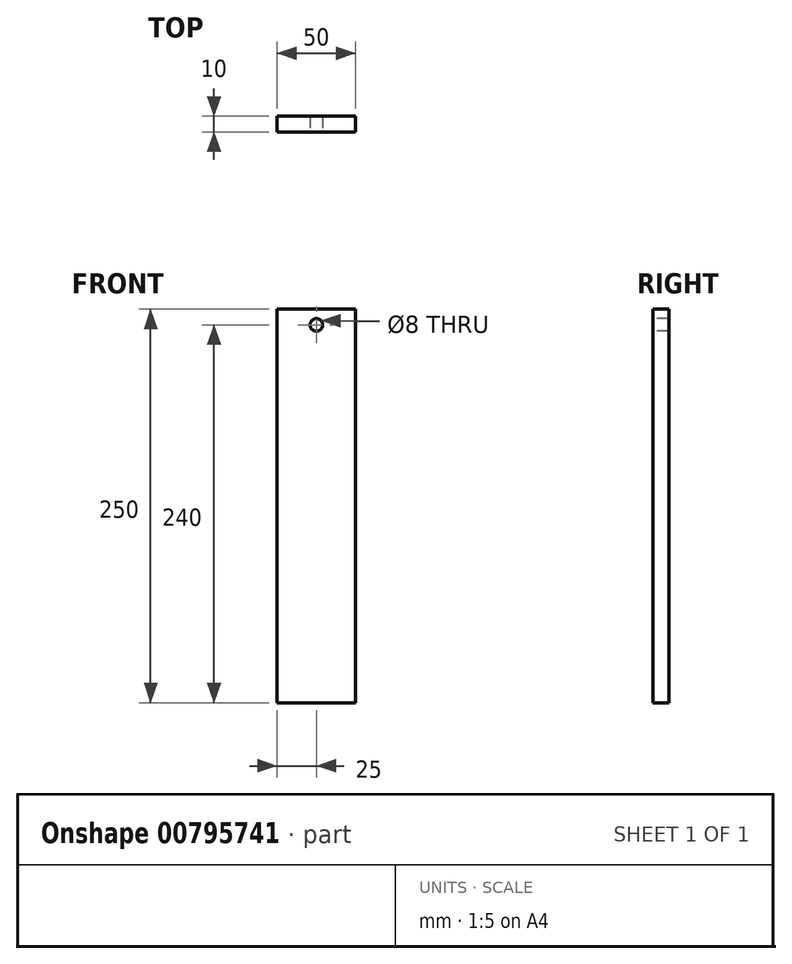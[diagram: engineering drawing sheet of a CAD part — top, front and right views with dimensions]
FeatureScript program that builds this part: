
annotation { "Feature Type Name" : "Feature", "Feature Type Description" : "" }
export const myFeature = defineFeature(function(context is Context, id is Id, definition is map)
    precondition{}
    {
        {
            var Q0;
            Q0=qCreatedBy(makeId("Front.planeOp"),FACE);
            var sketch = newSketch(context, id + "F0", { "sketchPlane" : qUnion([Q0])});
            skLineSegment(sketch, "E0.bottom", {"start": v(25, -125) * mm, "end": v(-25, -125) * mm});
            skLineSegment(sketch, "E0.top", {"start": v(25, 125) * mm, "end": v(-25, 125) * mm});
            skLineSegment(sketch, "E0.left", {"start": v(25, -125) * mm, "end": v(25, 125) * mm});
            skLineSegment(sketch, "E0.right", {"start": v(-25, -125) * mm, "end": v(-25, 125) * mm});
            skPoint(sketch, "E0.middle", {"position": v(0, 0) * mm});
            skSolve(sketch);
        }
        {
            var Q0;
            Q0=makeQuery(id+"F0.imprint","IMPRINT",FACE,{"disambiguationData":[TD([[makeQuery(id+"F0.imprint","IMPRINT",EDGE,{"derivedFrom":sQuery(id+"F0.wireOp",EDGE,"E0.bottom")}),-1.0]])]});
            extrude(context, id + "F1", {"entities" : qUnion([Q0]), "depth" : 10 * mm, "offsetDistance" : 25 * mm});
        }
        {
            var Q0;
            Q0=makeQuery(id+"F1.opExtrude","CAP_FACE",FACE,{"disambiguationData":[OSD([sQuery(id+"F0.wireOp",EDGE,"E0.bottom"),sQuery(id+"F0.wireOp",EDGE,"E0.top"),sQuery(id+"F0.wireOp",EDGE,"E0.left"),sQuery(id+"F0.wireOp",EDGE,"E0.right")])],"isStart":false});
            var sketch = newSketch(context, id + "F2", { "sketchPlane" : qUnion([Q0])});
            skLineSegment(sketch, "E1", {"start": v(0, 125) * mm, "end": v(0, 115) * mm, "construction": true});
            skCircle(sketch, "E2", {"center": v(0, 115) * mm, "radius": 4 * mm});
            skSolve(sketch);
        }
        {
            var Q0;
            Q0 = qSketchRegion(id + "F2", true);
            extrude(context, id + "F3", {"entities" : qUnion([Q0]), "operationType" : NewBodyOperationType.REMOVE, "endBound" : BoundingType.THROUGH_ALL, "oppositeDirection" : true, "depth" : 25 * mm, "offsetDistance" : 25 * mm});
        }
    });
